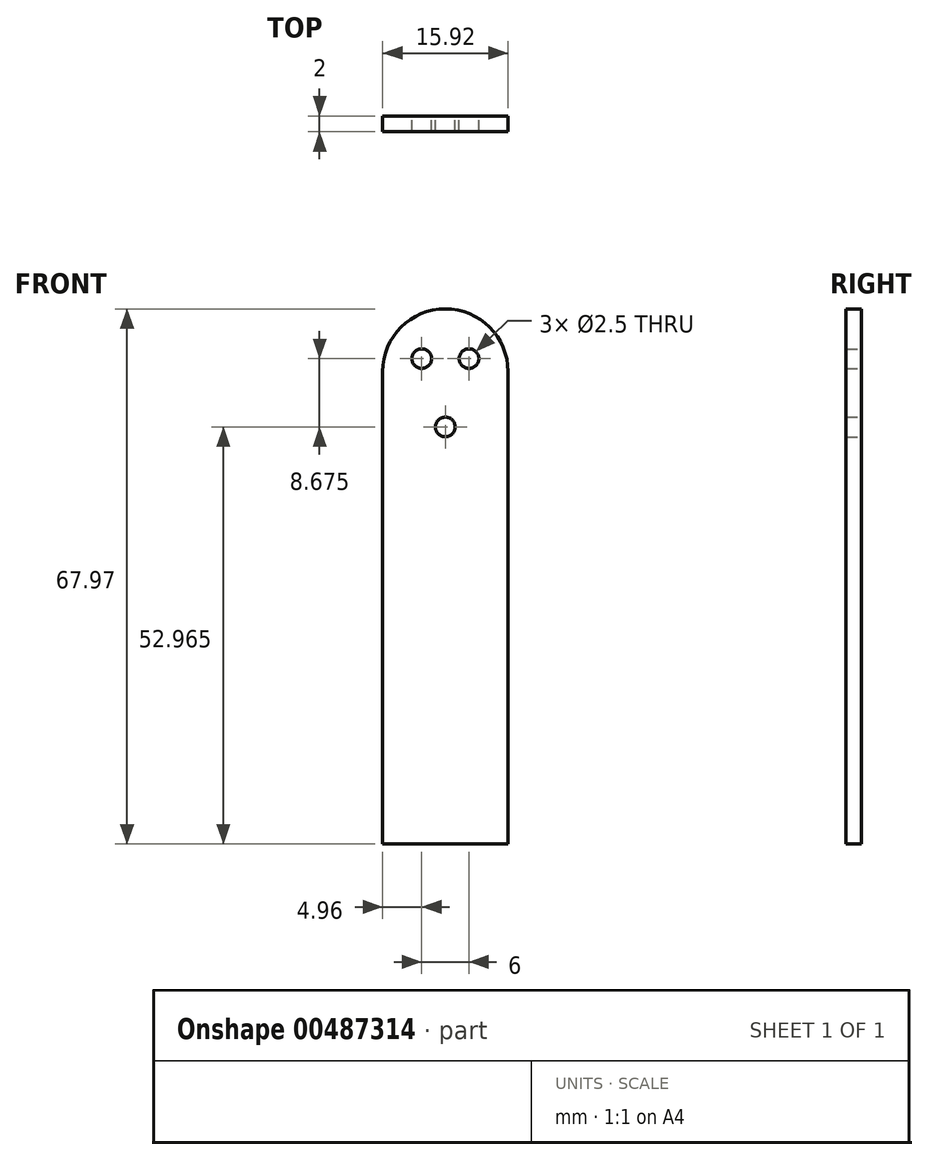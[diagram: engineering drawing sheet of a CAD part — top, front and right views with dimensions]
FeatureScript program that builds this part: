
annotation { "Feature Type Name" : "Feature", "Feature Type Description" : "" }
export const myFeature = defineFeature(function(context is Context, id is Id, definition is map)
    precondition{}
    {
        {
            var Q0;
            Q0=qCreatedBy(makeId("Front.planeOp"),FACE);
            var sketch = newSketch(context, id + "F0", { "sketchPlane" : qUnion([Q0])});
            skLineSegment(sketch, "E0.top", {"start": v(-7.96, -30) * mm, "end": v(7.96, -30) * mm});
            skLineSegment(sketch, "E0.left", {"start": v(-7.96, 30) * mm, "end": v(-7.96, -30) * mm});
            skLineSegment(sketch, "E0.right", {"start": v(7.96, 30) * mm, "end": v(7.96, -30) * mm});
            skPoint(sketch, "E0.middle", {"position": v(0, 0) * mm});
            skArc(sketch, "E1", {"start": v(7.96, 30) * mm, "mid": v(0, 37.97) * mm, "end": v(-7.96, 30) * mm});
            skCircle(sketch, "E2", {"center": v(0, 22.97) * mm, "radius": 1.25 * mm});
            skPoint(sketch, "E3", {"position": v(0, 37.97) * mm});
            skCircle(sketch, "E4", {"center": v(-3, 31.64) * mm, "radius": 1.25 * mm});
            skCircle(sketch, "E5.MirrorC", {"center": v(3, 31.64) * mm, "radius": 1.25 * mm});
            skSolve(sketch);
        }
        {
            var Q0;
            Q0=makeQuery(id+"F0.imprint","IMPRINT",FACE,{"disambiguationData":[TD([[makeQuery(id+"F0.imprint","IMPRINT",EDGE,{"derivedFrom":sQuery(id+"F0.wireOp",EDGE,"E0.top")}),1.0]])]});
            extrude(context, id + "F1", {"entities" : qUnion([Q0]), "endBound" : BoundingType.SYMMETRIC, "depth" : 2 * mm});
        }
    });
